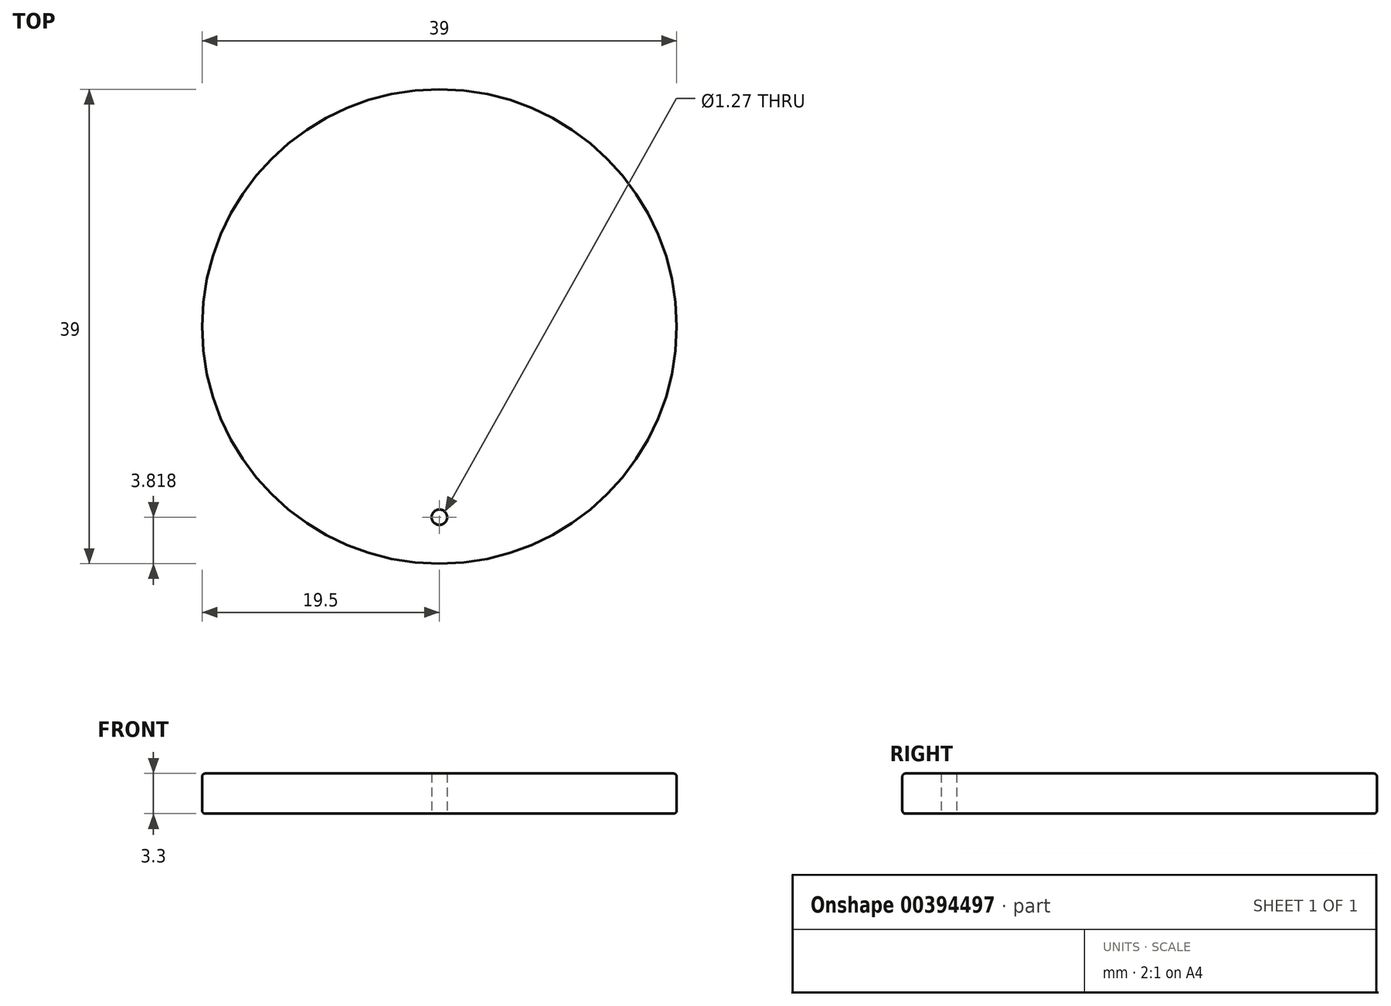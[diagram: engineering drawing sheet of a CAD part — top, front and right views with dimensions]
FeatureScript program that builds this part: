
annotation { "Feature Type Name" : "Feature", "Feature Type Description" : "" }
export const myFeature = defineFeature(function(context is Context, id is Id, definition is map)
    precondition{}
    {
        {
            var Q0;
            Q0=qCreatedBy(makeId("Top.planeOp"),FACE);
            var sketch = newSketch(context, id + "F0", { "sketchPlane" : qUnion([Q0])});
            skCircle(sketch, "E0", {"center": v(0, 0) * mm, "radius": 19.5 * mm});
            skSolve(sketch);
        }
        {
            var Q0;
            Q0=makeQuery(id+"F0.imprint","IMPRINT",FACE,{"disambiguationData":[TD([[makeQuery(id+"F0.imprint","IMPRINT",EDGE,{"derivedFrom":sQuery(id+"F0.wireOp",EDGE,"E0")}),1.0]])]});
            extrude(context, id + "F1", {"entities" : qUnion([Q0]), "depth" : 3.3 * mm});
        }
        {
            var Q0;
            Q0=makeQuery(id+"F1.opExtrude","CAP_EDGE",EDGE,{"disambiguationData":[OSD([sQuery(id+"F0.wireOp",EDGE,"E0")])],"isStart":false});
            var Q1;
            Q1=makeQuery(id+"F1.opExtrude","CAP_EDGE",EDGE,{"disambiguationData":[OSD([sQuery(id+"F0.wireOp",EDGE,"E0")])],"isStart":true});
            fillet(context, id + "F2", {"entities" : qUnion([Q0, Q1]), "radius" : 0.25 * mm, "tangentPropagation" : true, "allowEdgeOverflow" : false});
        }
        {
            var Q0;
            Q0=makeQuery(id+"F1.opExtrude","CAP_FACE",FACE,{"disambiguationData":[OSD([sQuery(id+"F0.wireOp",EDGE,"E0")])],"isStart":true});
            var sketch = newSketch(context, id + "F3", { "sketchPlane" : qUnion([Q0])});
            skCircle(sketch, "E1", {"center": v(0, 15.68) * mm, "radius": 0.64 * mm});
            skSolve(sketch);
        }
        {
            var Q0;
            Q0=makeQuery(id+"F3.imprint","IMPRINT",FACE,{"disambiguationData":[TD([[makeQuery(id+"F3.imprint","IMPRINT",EDGE,{"derivedFrom":sQuery(id+"F3.wireOp",EDGE,"E1")}),1.0]])]});
            extrude(context, id + "F4", {"entities" : qUnion([Q0]), "operationType" : NewBodyOperationType.REMOVE, "oppositeDirection" : true, "depth" : 4 * mm});
        }
    });
